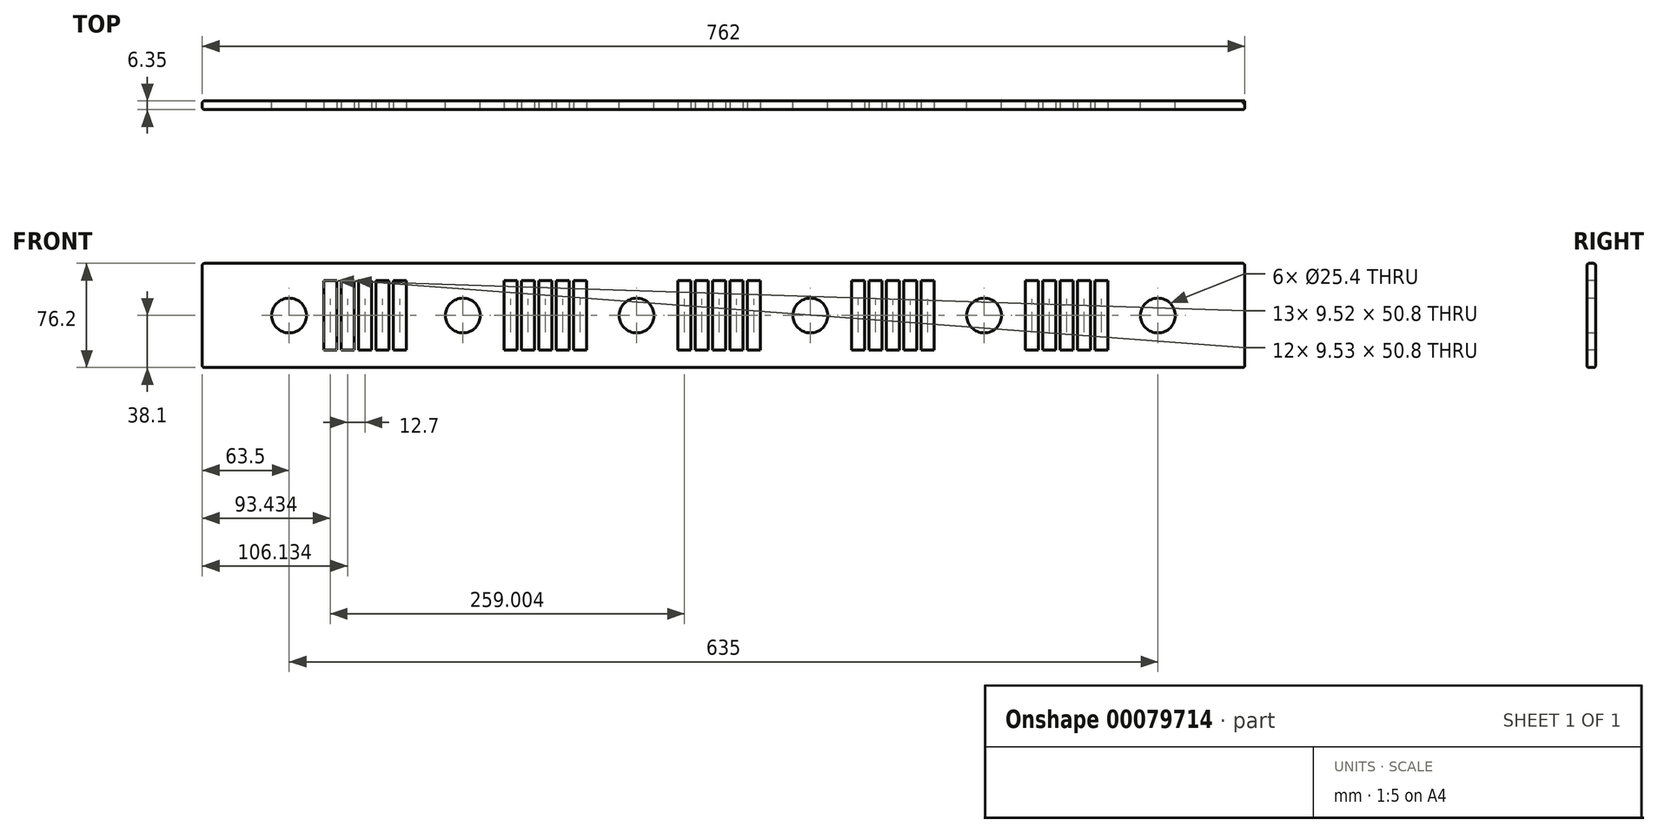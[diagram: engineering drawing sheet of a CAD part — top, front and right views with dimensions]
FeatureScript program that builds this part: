
annotation { "Feature Type Name" : "Feature", "Feature Type Description" : "" }
export const myFeature = defineFeature(function(context is Context, id is Id, definition is map)
    precondition{}
    {
        {
            var Q0;
            Q0=qCreatedBy(makeId("Front.planeOp"),FACE);
            var sketch = newSketch(context, id + "F0", { "sketchPlane" : qUnion([Q0])});
            skLineSegment(sketch, "E0.bottom", {"start": v(0, 0) * mm, "end": v(762, 0) * mm});
            skLineSegment(sketch, "E0.top", {"start": v(0, 76.2) * mm, "end": v(762, 76.2) * mm});
            skLineSegment(sketch, "E0.left", {"start": v(0, 0) * mm, "end": v(0, 76.2) * mm});
            skLineSegment(sketch, "E0.right", {"start": v(762, 0) * mm, "end": v(762, 76.2) * mm});
            skCircle(sketch, "E1", {"center": v(63.5, 38.1) * mm, "radius": 12.7 * mm});
            skPoint(sketch, "E1.centerSnap0", {"position": v(0, 38.1) * mm});
            skCircle(sketch, "E2", {"center": v(190.5, 38.1) * mm, "radius": 12.7 * mm});
            skCircle(sketch, "E3", {"center": v(317.5, 38.1) * mm, "radius": 12.7 * mm});
            skCircle(sketch, "E4", {"center": v(444.5, 38.1) * mm, "radius": 12.7 * mm});
            skCircle(sketch, "E5", {"center": v(571.5, 38.1) * mm, "radius": 12.7 * mm});
            skCircle(sketch, "E6", {"center": v(698.5, 38.1) * mm, "radius": 12.7 * mm});
            skSolve(sketch);
        }
        {
            var Q0;
            Q0 = qSketchRegion(id + "F0", true);
            extrude(context, id + "F1", {"entities" : qUnion([Q0]), "depth" : 6.35 * mm});
        }
        {
            var Q0;
            Q0=makeQuery(id+"F1.opExtrude","CAP_FACE",FACE,{"disambiguationData":[OSD([sQuery(id+"F0.wireOp",EDGE,"E0.bottom"),sQuery(id+"F0.wireOp",EDGE,"E0.top"),sQuery(id+"F0.wireOp",EDGE,"E0.left"),sQuery(id+"F0.wireOp",EDGE,"E0.right"),sQuery(id+"F0.wireOp",EDGE,"E1"),sQuery(id+"F0.wireOp",EDGE,"E2"),sQuery(id+"F0.wireOp",EDGE,"E3"),sQuery(id+"F0.wireOp",EDGE,"E4"),sQuery(id+"F0.wireOp",EDGE,"E5"),sQuery(id+"F0.wireOp",EDGE,"E6")])],"isStart":false});
            var sketch = newSketch(context, id + "F2", { "sketchPlane" : qUnion([Q0])});
            skLineSegment(sketch, "E7.bottom", {"start": v(88.67, 12.7) * mm, "end": v(98.2, 12.7) * mm});
            skLineSegment(sketch, "E7.top", {"start": v(88.67, 63.5) * mm, "end": v(98.2, 63.5) * mm});
            skLineSegment(sketch, "E7.left", {"start": v(98.2, 12.7) * mm, "end": v(98.2, 63.5) * mm});
            skLineSegment(sketch, "E7.right", {"start": v(88.67, 12.7) * mm, "end": v(88.67, 63.5) * mm});
            skLineSegment(sketch, "E8.1.0.0", {"start": v(101.37, 12.7) * mm, "end": v(110.9, 12.7) * mm});
            skLineSegment(sketch, "E8.1.0.1", {"start": v(101.37, 63.5) * mm, "end": v(110.9, 63.5) * mm});
            skLineSegment(sketch, "E8.1.0.2", {"start": v(110.9, 12.7) * mm, "end": v(110.9, 63.5) * mm});
            skLineSegment(sketch, "E8.1.0.3", {"start": v(101.37, 12.7) * mm, "end": v(101.37, 63.5) * mm});
            skLineSegment(sketch, "E8.2.0.0", {"start": v(114.07, 12.7) * mm, "end": v(123.6, 12.7) * mm});
            skLineSegment(sketch, "E8.2.0.1", {"start": v(114.07, 63.5) * mm, "end": v(123.6, 63.5) * mm});
            skLineSegment(sketch, "E8.2.0.2", {"start": v(123.6, 12.7) * mm, "end": v(123.6, 63.5) * mm});
            skLineSegment(sketch, "E8.2.0.3", {"start": v(114.07, 12.7) * mm, "end": v(114.07, 63.5) * mm});
            skLineSegment(sketch, "E8.3.0.0", {"start": v(126.77, 12.7) * mm, "end": v(136.3, 12.7) * mm});
            skLineSegment(sketch, "E8.3.0.1", {"start": v(126.77, 63.5) * mm, "end": v(136.3, 63.5) * mm});
            skLineSegment(sketch, "E8.3.0.2", {"start": v(136.3, 12.7) * mm, "end": v(136.3, 63.5) * mm});
            skLineSegment(sketch, "E8.3.0.3", {"start": v(126.77, 12.7) * mm, "end": v(126.77, 63.5) * mm});
            skLineSegment(sketch, "E8.4.0.0", {"start": v(139.47, 12.7) * mm, "end": v(149, 12.7) * mm});
            skLineSegment(sketch, "E8.4.0.1", {"start": v(139.47, 63.5) * mm, "end": v(149, 63.5) * mm});
            skLineSegment(sketch, "E8.4.0.2", {"start": v(149, 12.7) * mm, "end": v(149, 63.5) * mm});
            skLineSegment(sketch, "E8.4.0.3", {"start": v(139.47, 12.7) * mm, "end": v(139.47, 63.5) * mm});
            skLineSegment(sketch, "E8.direction1", {"start": v(98.2, 12.7) * mm, "end": v(110.9, 12.7) * mm, "construction": true});
            skLineSegment(sketch, "E9.bottom", {"start": v(220.68, 12.7) * mm, "end": v(230.2, 12.7) * mm});
            skLineSegment(sketch, "E9.top", {"start": v(220.68, 63.5) * mm, "end": v(230.2, 63.5) * mm});
            skLineSegment(sketch, "E9.left", {"start": v(220.68, 12.7) * mm, "end": v(220.68, 63.5) * mm});
            skLineSegment(sketch, "E9.right", {"start": v(230.2, 12.7) * mm, "end": v(230.2, 63.5) * mm});
            skLineSegment(sketch, "E10.1.0.0", {"start": v(242.9, 12.7) * mm, "end": v(242.9, 63.5) * mm});
            skLineSegment(sketch, "E10.1.0.1", {"start": v(233.38, 12.7) * mm, "end": v(233.38, 63.5) * mm});
            skLineSegment(sketch, "E10.1.0.2", {"start": v(233.38, 63.5) * mm, "end": v(242.9, 63.5) * mm});
            skLineSegment(sketch, "E10.1.0.3", {"start": v(233.38, 12.7) * mm, "end": v(242.9, 12.7) * mm});
            skLineSegment(sketch, "E10.2.0.0", {"start": v(255.6, 12.7) * mm, "end": v(255.6, 63.5) * mm});
            skLineSegment(sketch, "E10.2.0.1", {"start": v(246.08, 12.7) * mm, "end": v(246.08, 63.5) * mm});
            skLineSegment(sketch, "E10.2.0.2", {"start": v(246.08, 63.5) * mm, "end": v(255.6, 63.5) * mm});
            skLineSegment(sketch, "E10.2.0.3", {"start": v(246.08, 12.7) * mm, "end": v(255.6, 12.7) * mm});
            skLineSegment(sketch, "E10.3.0.0", {"start": v(268.3, 12.7) * mm, "end": v(268.3, 63.5) * mm});
            skLineSegment(sketch, "E10.3.0.1", {"start": v(258.78, 12.7) * mm, "end": v(258.78, 63.5) * mm});
            skLineSegment(sketch, "E10.3.0.2", {"start": v(258.78, 63.5) * mm, "end": v(268.3, 63.5) * mm});
            skLineSegment(sketch, "E10.3.0.3", {"start": v(258.78, 12.7) * mm, "end": v(268.3, 12.7) * mm});
            skLineSegment(sketch, "E10.4.0.0", {"start": v(281, 12.7) * mm, "end": v(281, 63.5) * mm});
            skLineSegment(sketch, "E10.4.0.1", {"start": v(271.48, 12.7) * mm, "end": v(271.48, 63.5) * mm});
            skLineSegment(sketch, "E10.4.0.2", {"start": v(271.48, 63.5) * mm, "end": v(281, 63.5) * mm});
            skLineSegment(sketch, "E10.4.0.3", {"start": v(271.48, 12.7) * mm, "end": v(281, 12.7) * mm});
            skLineSegment(sketch, "E10.direction1", {"start": v(230.2, 12.7) * mm, "end": v(242.9, 12.7) * mm, "construction": true});
            skLineSegment(sketch, "E11.bottom", {"start": v(347.68, 12.7) * mm, "end": v(357.2, 12.7) * mm});
            skLineSegment(sketch, "E11.top", {"start": v(347.68, 63.5) * mm, "end": v(357.2, 63.5) * mm});
            skLineSegment(sketch, "E11.left", {"start": v(347.68, 12.7) * mm, "end": v(347.68, 63.5) * mm});
            skLineSegment(sketch, "E11.right", {"start": v(357.2, 12.7) * mm, "end": v(357.2, 63.5) * mm});
            skLineSegment(sketch, "E12.1.0.0", {"start": v(369.9, 12.7) * mm, "end": v(369.9, 63.5) * mm});
            skLineSegment(sketch, "E12.1.0.1", {"start": v(360.38, 12.7) * mm, "end": v(369.9, 12.7) * mm});
            skLineSegment(sketch, "E12.1.0.2", {"start": v(360.38, 12.7) * mm, "end": v(360.38, 63.5) * mm});
            skLineSegment(sketch, "E12.1.0.3", {"start": v(360.38, 63.5) * mm, "end": v(369.9, 63.5) * mm});
            skLineSegment(sketch, "E12.2.0.0", {"start": v(382.6, 12.7) * mm, "end": v(382.6, 63.5) * mm});
            skLineSegment(sketch, "E12.2.0.1", {"start": v(373.08, 12.7) * mm, "end": v(382.6, 12.7) * mm});
            skLineSegment(sketch, "E12.2.0.2", {"start": v(373.08, 12.7) * mm, "end": v(373.08, 63.5) * mm});
            skLineSegment(sketch, "E12.2.0.3", {"start": v(373.08, 63.5) * mm, "end": v(382.6, 63.5) * mm});
            skLineSegment(sketch, "E12.3.0.0", {"start": v(395.3, 12.7) * mm, "end": v(395.3, 63.5) * mm});
            skLineSegment(sketch, "E12.3.0.1", {"start": v(385.78, 12.7) * mm, "end": v(395.3, 12.7) * mm});
            skLineSegment(sketch, "E12.3.0.2", {"start": v(385.78, 12.7) * mm, "end": v(385.78, 63.5) * mm});
            skLineSegment(sketch, "E12.3.0.3", {"start": v(385.78, 63.5) * mm, "end": v(395.3, 63.5) * mm});
            skLineSegment(sketch, "E12.4.0.0", {"start": v(408, 12.7) * mm, "end": v(408, 63.5) * mm});
            skLineSegment(sketch, "E12.4.0.1", {"start": v(398.48, 12.7) * mm, "end": v(408, 12.7) * mm});
            skLineSegment(sketch, "E12.4.0.2", {"start": v(398.48, 12.7) * mm, "end": v(398.48, 63.5) * mm});
            skLineSegment(sketch, "E12.4.0.3", {"start": v(398.48, 63.5) * mm, "end": v(408, 63.5) * mm});
            skLineSegment(sketch, "E12.direction1", {"start": v(357.2, 12.7) * mm, "end": v(369.9, 12.7) * mm, "construction": true});
            skLineSegment(sketch, "E13.bottom", {"start": v(474.68, 12.7) * mm, "end": v(484.2, 12.7) * mm});
            skLineSegment(sketch, "E13.top", {"start": v(474.68, 63.5) * mm, "end": v(484.2, 63.5) * mm});
            skLineSegment(sketch, "E13.left", {"start": v(474.68, 12.7) * mm, "end": v(474.68, 63.5) * mm});
            skLineSegment(sketch, "E13.right", {"start": v(484.2, 12.7) * mm, "end": v(484.2, 63.5) * mm});
            skLineSegment(sketch, "E14.1.0.0", {"start": v(487.38, 12.7) * mm, "end": v(487.38, 63.5) * mm});
            skLineSegment(sketch, "E14.1.0.1", {"start": v(496.9, 12.7) * mm, "end": v(496.9, 63.5) * mm});
            skLineSegment(sketch, "E14.1.0.2", {"start": v(487.38, 12.7) * mm, "end": v(496.9, 12.7) * mm});
            skLineSegment(sketch, "E14.1.0.3", {"start": v(487.38, 63.5) * mm, "end": v(496.9, 63.5) * mm});
            skLineSegment(sketch, "E14.2.0.0", {"start": v(500.08, 12.7) * mm, "end": v(500.08, 63.5) * mm});
            skLineSegment(sketch, "E14.2.0.1", {"start": v(509.6, 12.7) * mm, "end": v(509.6, 63.5) * mm});
            skLineSegment(sketch, "E14.2.0.2", {"start": v(500.08, 12.7) * mm, "end": v(509.6, 12.7) * mm});
            skLineSegment(sketch, "E14.2.0.3", {"start": v(500.08, 63.5) * mm, "end": v(509.6, 63.5) * mm});
            skLineSegment(sketch, "E14.3.0.0", {"start": v(512.78, 12.7) * mm, "end": v(512.78, 63.5) * mm});
            skLineSegment(sketch, "E14.3.0.1", {"start": v(522.3, 12.7) * mm, "end": v(522.3, 63.5) * mm});
            skLineSegment(sketch, "E14.3.0.2", {"start": v(512.78, 12.7) * mm, "end": v(522.3, 12.7) * mm});
            skLineSegment(sketch, "E14.3.0.3", {"start": v(512.78, 63.5) * mm, "end": v(522.3, 63.5) * mm});
            skLineSegment(sketch, "E14.4.0.0", {"start": v(525.48, 12.7) * mm, "end": v(525.48, 63.5) * mm});
            skLineSegment(sketch, "E14.4.0.1", {"start": v(535, 12.7) * mm, "end": v(535, 63.5) * mm});
            skLineSegment(sketch, "E14.4.0.2", {"start": v(525.48, 12.7) * mm, "end": v(535, 12.7) * mm});
            skLineSegment(sketch, "E14.4.0.3", {"start": v(525.48, 63.5) * mm, "end": v(535, 63.5) * mm});
            skLineSegment(sketch, "E14.direction1", {"start": v(474.68, 12.7) * mm, "end": v(487.38, 12.7) * mm, "construction": true});
            skLineSegment(sketch, "E15.bottom", {"start": v(601.68, 12.7) * mm, "end": v(611.2, 12.7) * mm});
            skLineSegment(sketch, "E15.top", {"start": v(601.68, 63.5) * mm, "end": v(611.2, 63.5) * mm});
            skLineSegment(sketch, "E15.left", {"start": v(601.68, 12.7) * mm, "end": v(601.68, 63.5) * mm});
            skLineSegment(sketch, "E15.right", {"start": v(611.2, 12.7) * mm, "end": v(611.2, 63.5) * mm});
            skLineSegment(sketch, "E16.1.0.0", {"start": v(614.38, 12.7) * mm, "end": v(623.9, 12.7) * mm});
            skLineSegment(sketch, "E16.1.0.1", {"start": v(614.38, 12.7) * mm, "end": v(614.38, 63.5) * mm});
            skLineSegment(sketch, "E16.1.0.2", {"start": v(623.9, 12.7) * mm, "end": v(623.9, 63.5) * mm});
            skLineSegment(sketch, "E16.1.0.3", {"start": v(614.38, 63.5) * mm, "end": v(623.9, 63.5) * mm});
            skLineSegment(sketch, "E16.2.0.0", {"start": v(627.08, 12.7) * mm, "end": v(636.6, 12.7) * mm});
            skLineSegment(sketch, "E16.2.0.1", {"start": v(627.08, 12.7) * mm, "end": v(627.08, 63.5) * mm});
            skLineSegment(sketch, "E16.2.0.2", {"start": v(636.6, 12.7) * mm, "end": v(636.6, 63.5) * mm});
            skLineSegment(sketch, "E16.2.0.3", {"start": v(627.08, 63.5) * mm, "end": v(636.6, 63.5) * mm});
            skLineSegment(sketch, "E16.3.0.0", {"start": v(639.78, 12.7) * mm, "end": v(649.3, 12.7) * mm});
            skLineSegment(sketch, "E16.3.0.1", {"start": v(639.78, 12.7) * mm, "end": v(639.78, 63.5) * mm});
            skLineSegment(sketch, "E16.3.0.2", {"start": v(649.3, 12.7) * mm, "end": v(649.3, 63.5) * mm});
            skLineSegment(sketch, "E16.3.0.3", {"start": v(639.78, 63.5) * mm, "end": v(649.3, 63.5) * mm});
            skLineSegment(sketch, "E16.4.0.0", {"start": v(652.48, 12.7) * mm, "end": v(662, 12.7) * mm});
            skLineSegment(sketch, "E16.4.0.1", {"start": v(652.48, 12.7) * mm, "end": v(652.48, 63.5) * mm});
            skLineSegment(sketch, "E16.4.0.2", {"start": v(662, 12.7) * mm, "end": v(662, 63.5) * mm});
            skLineSegment(sketch, "E16.4.0.3", {"start": v(652.48, 63.5) * mm, "end": v(662, 63.5) * mm});
            skLineSegment(sketch, "E16.direction1", {"start": v(601.68, 12.7) * mm, "end": v(614.38, 12.7) * mm, "construction": true});
            skSolve(sketch);
        }
        {
            var Q0;
            Q0 = qSketchRegion(id + "F2", true);
            extrude(context, id + "F3", {"entities" : qUnion([Q0]), "operationType" : NewBodyOperationType.REMOVE, "endBound" : BoundingType.THROUGH_ALL, "oppositeDirection" : true, "depth" : 25.4 * mm});
        }
        {
            var Q0;
            Q0=makeQuery(id+"F1.opExtrude","CAP_EDGE",EDGE,{"disambiguationData":[OSD([sQuery(id+"F0.wireOp",EDGE,"E0.top")])],"isStart":false});
            var Q1;
            Q1=makeQuery(id+"F1.opExtrude","CAP_EDGE",EDGE,{"disambiguationData":[OSD([sQuery(id+"F0.wireOp",EDGE,"E0.top")])],"isStart":true});
            var Q2;
            Q2=makeQuery(id+"F1.opExtrude","CAP_EDGE",EDGE,{"disambiguationData":[OSD([sQuery(id+"F0.wireOp",EDGE,"E0.left")])],"isStart":false});
            var Q3;
            Q3=makeQuery(id+"F1.opExtrude","CAP_EDGE",EDGE,{"disambiguationData":[OSD([sQuery(id+"F0.wireOp",EDGE,"E0.left")])],"isStart":true});
            var Q4;
            Q4=makeQuery(id+"F1.opExtrude","SWEPT_FACE",FACE,{"disambiguationData":[OSD([sQuery(id+"F0.wireOp",EDGE,"E0.top")])]});
            var Q5;
            Q5=makeQuery(id+"F1.opExtrude","SWEPT_EDGE",EDGE,{"disambiguationData":[OSD([sQuery(id+"F0.wireOp",EDGE,"E0.bottom"),sQuery(id+"F0.wireOp",EDGE,"E0.left")])]});
            var Q6;
            Q6=makeQuery(id+"F1.opExtrude","CAP_EDGE",EDGE,{"disambiguationData":[OSD([sQuery(id+"F0.wireOp",EDGE,"E0.bottom")])],"isStart":false});
            var Q7;
            Q7=makeQuery(id+"F1.opExtrude","CAP_EDGE",EDGE,{"disambiguationData":[OSD([sQuery(id+"F0.wireOp",EDGE,"E0.bottom")])],"isStart":true});
            var Q8;
            Q8=makeQuery(id+"F1.opExtrude","SWEPT_EDGE",EDGE,{"disambiguationData":[OSD([sQuery(id+"F0.wireOp",EDGE,"E0.bottom"),sQuery(id+"F0.wireOp",EDGE,"E0.right")])]});
            var Q9;
            Q9=makeQuery(id+"F1.opExtrude","CAP_EDGE",EDGE,{"disambiguationData":[OSD([sQuery(id+"F0.wireOp",EDGE,"E0.right")])],"isStart":false});
            var Q10;
            Q10=makeQuery(id+"F1.opExtrude","SWEPT_EDGE",EDGE,{"disambiguationData":[OSD([sQuery(id+"F0.wireOp",EDGE,"E0.top"),sQuery(id+"F0.wireOp",EDGE,"E0.right")])]});
            fillet(context, id + "F4", {"entities" : qUnion([Q0, Q1, Q2, Q3, Q4, Q5, Q6, Q7, Q8, Q9, Q10]), "radius" : 1.6 * mm, "tangentPropagation" : true, "allowEdgeOverflow" : false});
        }
    });
